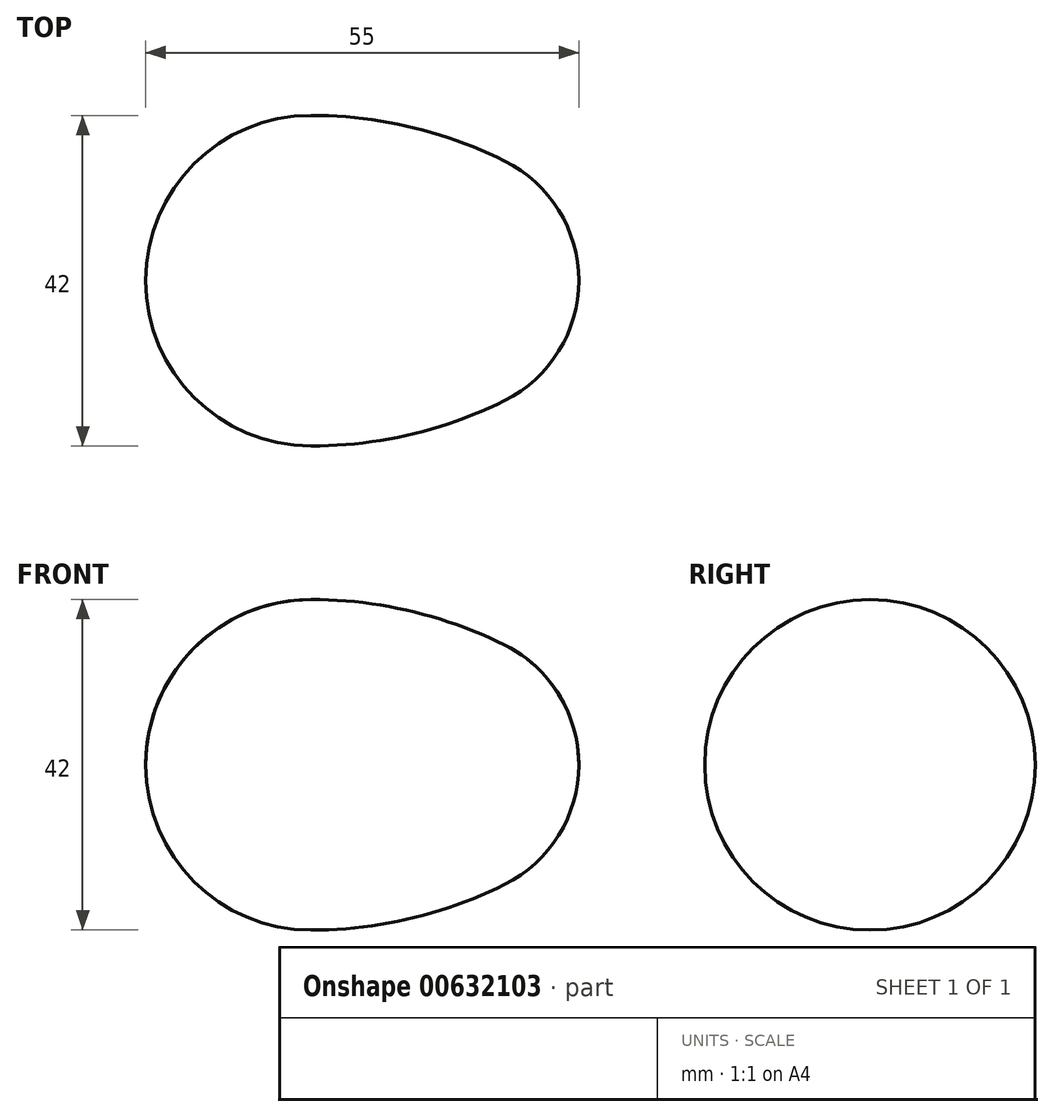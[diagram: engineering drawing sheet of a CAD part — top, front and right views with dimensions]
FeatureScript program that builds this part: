
annotation { "Feature Type Name" : "Feature", "Feature Type Description" : "" }
export const myFeature = defineFeature(function(context is Context, id is Id, definition is map)
    precondition{}
    {
        {
            var Q0;
            Q0=qCreatedBy(makeId("Front.planeOp"),FACE);
            var sketch = newSketch(context, id + "F0", { "sketchPlane" : qUnion([Q0])});
            skArc(sketch, "E0", {"start": v(0, 21) * mm, "mid": v(-21, 0) * mm, "end": v(0, -21) * mm});
            skPoint(sketch, "E1", {"position": v(17, 0) * mm});
            skLineSegment(sketch, "E2", {"start": v(0, 21) * mm, "end": v(13.4, 4.45) * mm, "construction": true});
            skLineSegment(sketch, "E3", {"start": v(0, -21) * mm, "end": v(23.13, 7.57) * mm, "construction": true});
            skArc(sketch, "E4", {"start": v(27.7, -13.21) * mm, "mid": v(33.9, 1.85) * mm, "end": v(24.58, 15.22) * mm});
            skArc(sketch, "E5", {"start": v(24.58, 15.22) * mm, "mid": v(12.63, 19.53) * mm, "end": v(0, 21) * mm});
            skArc(sketch, "E6", {"start": v(0, -21) * mm, "mid": v(14.65, -19.96) * mm, "end": v(27.7, -13.21) * mm});
            skLineSegment(sketch, "E7", {"start": v(-26.59, 0) * mm, "end": v(43.12, 0) * mm, "construction": true});
            skLineSegment(sketch, "E8", {"start": v(-21, 0) * mm, "end": v(34, 0) * mm});
            skSolve(sketch);
        }
        {
            var Q0;
            {var subQ0=sQuery(id+"F0.wireOp",EDGE,"E5");Q0=makeQuery(id+"F0.imprint","IMPRINT",FACE,{"disambiguationData":[TD([[makeQuery(id+"F0.imprint","IMPRINT",EDGE,{"derivedFrom":subQ0}),1.0]])]});}
            var Q1;
            Q1=sQuery(id+"F0.wireOp",EDGE,"E8");
            revolve(context, id + "F1", {"entities" : qUnion([Q0]), "axis" : qUnion([Q1]), "revolveType" : RevolveType.FULL});
        }
    });
